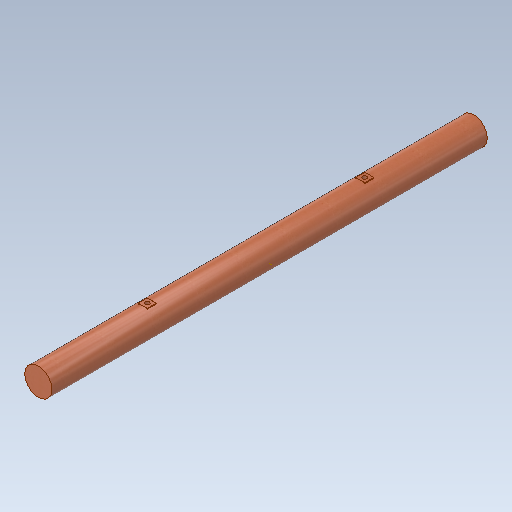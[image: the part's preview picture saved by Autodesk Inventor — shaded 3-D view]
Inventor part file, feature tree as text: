
AUTODESK INVENTOR PART (.ipt)
format: ipt  version: 2020.1 (Build 241239000, 239)  size: 143,360 bytes
history: native  units: in
note: dims shown in document units (in); Inventor stores cm internally (conversion verified against a paired STEP export)
features: sketch x3, extrude x2, plane x1, mirror x1, hole x1
ambient origin geometry x8: Origin, YZ Plane, XZ Plane, XY Plane, X Axis, Y Axis, Z Axis, Center Point
bodies: Solid1 (feature_tree)
feature tree (8):
  extrude  "Extrusion1"  Depth=96.0in TaperAngle=0.0deg
  plane  "Work Plane2"
  extrude  "Extrusion3"  Depth=2.0in
  mirror  "Mirror1"
  hole  "Hole2"  [1 undecoded]
  sketch  "Sketch1"  dims[d0=6.0in d1=96.0in d2=0.0in]
  sketch  "Sketch4"  dims[d16=3.0in d17=2.0in]
  sketch  "Sketch5"  dims[d19=24.0in d20=1.0in d21=0.0in d22=24.0in d23=24.0in d24=1.0in d25=0.75in d26=0.625in d27=0.19in d28=0.5635in d29=1.0in d30=0.8108in]
note: 1 required parameter value undecoded (feature->parameter linkage not recoverable at this tier; creation-order binding heuristic only, values carry confidence <= 0.55)
